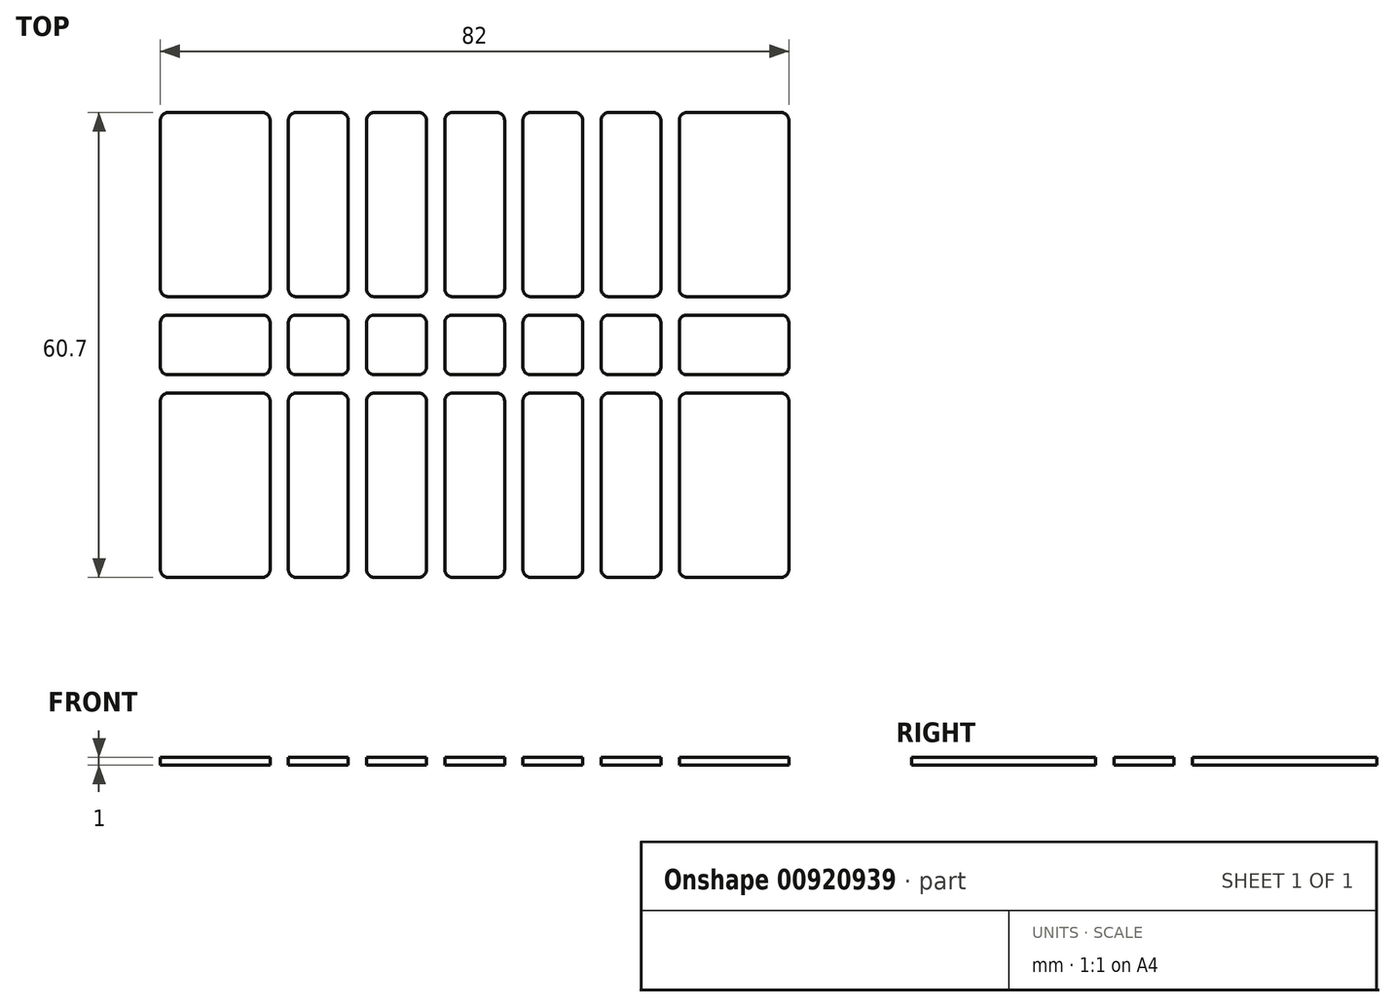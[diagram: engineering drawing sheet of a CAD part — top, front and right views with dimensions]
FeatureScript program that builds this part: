
annotation { "Feature Type Name" : "Feature", "Feature Type Description" : "" }
export const myFeature = defineFeature(function(context is Context, id is Id, definition is map)
    precondition{}
    {
        {
            var Q0;
            Q0=qCreatedBy(makeId("Top.planeOp"),FACE);
            var sketch = newSketch(context, id + "F0", { "sketchPlane" : qUnion([Q0])});
            skLineSegment(sketch, "E0.bottom", {"start": v(44, 33.35) * mm, "end": v(-44, 33.35) * mm, "construction": true});
            skLineSegment(sketch, "E0.top", {"start": v(44, -33.35) * mm, "end": v(-44, -33.35) * mm, "construction": true});
            skLineSegment(sketch, "E0.left", {"start": v(44, 33.35) * mm, "end": v(44, -33.35) * mm, "construction": true});
            skLineSegment(sketch, "E0.right", {"start": v(-44, 33.35) * mm, "end": v(-44, -33.35) * mm, "construction": true});
            skLineSegment(sketch, "E1", {"start": v(0, 0) * mm, "end": v(0, -33.35) * mm, "construction": true});
            skLineSegment(sketch, "E2", {"start": v(-5.1, 0) * mm, "end": v(-5.1, -33.35) * mm, "construction": true});
            skLineSegment(sketch, "E3", {"start": v(-15.3, 0) * mm, "end": v(-15.3, -33.35) * mm, "construction": true});
            skLineSegment(sketch, "E4", {"start": v(-25.5, 0) * mm, "end": v(-25.5, -33.35) * mm, "construction": true});
            skLineSegment(sketch, "E5.MirrorCS", {"start": v(5.1, 0) * mm, "end": v(5.1, -33.35) * mm, "construction": true});
            skLineSegment(sketch, "E6", {"start": v(0, 0) * mm, "end": v(-44, 0) * mm, "construction": true});
            skLineSegment(sketch, "E7", {"start": v(0, -5.1) * mm, "end": v(-44, -5.1) * mm, "construction": true});
            skLineSegment(sketch, "E8.MirrorCS", {"start": v(0, 5.1) * mm, "end": v(-44, 5.1) * mm, "construction": true});
            skLineSegment(sketch, "E9.bottom", {"start": v(-40, -6.3) * mm, "end": v(-27.7, -6.3) * mm});
            skLineSegment(sketch, "E9.top", {"start": v(-40, -30.35) * mm, "end": v(-27.7, -30.35) * mm});
            skLineSegment(sketch, "E9.left", {"start": v(-41, -7.3) * mm, "end": v(-41, -29.35) * mm});
            skLineSegment(sketch, "E9.right", {"start": v(-26.7, -7.3) * mm, "end": v(-26.7, -29.35) * mm});
            skLineSegment(sketch, "E10.bottom", {"start": v(-23.3, -6.3) * mm, "end": v(-17.5, -6.3) * mm});
            skLineSegment(sketch, "E10.top", {"start": v(-23.3, -30.35) * mm, "end": v(-17.5, -30.35) * mm});
            skLineSegment(sketch, "E10.left", {"start": v(-24.3, -7.3) * mm, "end": v(-24.3, -29.35) * mm});
            skLineSegment(sketch, "E10.right", {"start": v(-16.5, -7.3) * mm, "end": v(-16.5, -29.35) * mm});
            skLineSegment(sketch, "E11.bottom", {"start": v(-13.1, -6.3) * mm, "end": v(-7.3, -6.3) * mm});
            skLineSegment(sketch, "E11.top", {"start": v(-13.1, -30.35) * mm, "end": v(-7.3, -30.35) * mm});
            skLineSegment(sketch, "E11.left", {"start": v(-14.1, -7.3) * mm, "end": v(-14.1, -29.35) * mm});
            skLineSegment(sketch, "E11.right", {"start": v(-6.3, -7.3) * mm, "end": v(-6.3, -29.35) * mm});
            skLineSegment(sketch, "E12.bottom", {"start": v(-2.9, -6.3) * mm, "end": v(2.9, -6.3) * mm});
            skLineSegment(sketch, "E12.top", {"start": v(-2.9, -30.35) * mm, "end": v(2.9, -30.35) * mm});
            skLineSegment(sketch, "E12.left", {"start": v(-3.9, -7.3) * mm, "end": v(-3.9, -29.35) * mm});
            skLineSegment(sketch, "E12.right", {"start": v(3.9, -7.3) * mm, "end": v(3.9, -29.35) * mm});
            skLineSegment(sketch, "E13.bottom", {"start": v(-40, 3.9) * mm, "end": v(-27.7, 3.9) * mm});
            skLineSegment(sketch, "E13.top", {"start": v(-40, -3.9) * mm, "end": v(-27.7, -3.9) * mm});
            skLineSegment(sketch, "E13.left", {"start": v(-41, 2.9) * mm, "end": v(-41, -2.9) * mm});
            skLineSegment(sketch, "E13.right", {"start": v(-26.7, 2.9) * mm, "end": v(-26.7, -2.9) * mm});
            skLineSegment(sketch, "E14.bottom", {"start": v(-23.3, 3.9) * mm, "end": v(-17.5, 3.9) * mm});
            skLineSegment(sketch, "E14.top", {"start": v(-23.3, -3.9) * mm, "end": v(-17.5, -3.9) * mm});
            skLineSegment(sketch, "E14.left", {"start": v(-24.3, 2.9) * mm, "end": v(-24.3, -2.9) * mm});
            skLineSegment(sketch, "E14.right", {"start": v(-16.5, 2.9) * mm, "end": v(-16.5, -2.9) * mm});
            skLineSegment(sketch, "E15.bottom", {"start": v(-13.1, 3.9) * mm, "end": v(-7.3, 3.9) * mm});
            skLineSegment(sketch, "E15.top", {"start": v(-13.1, -3.9) * mm, "end": v(-7.3, -3.9) * mm});
            skLineSegment(sketch, "E15.left", {"start": v(-14.1, 2.9) * mm, "end": v(-14.1, -2.9) * mm});
            skLineSegment(sketch, "E15.right", {"start": v(-6.3, 2.9) * mm, "end": v(-6.3, -2.9) * mm});
            skLineSegment(sketch, "E16.bottom", {"start": v(-2.9, 3.9) * mm, "end": v(2.9, 3.9) * mm});
            skLineSegment(sketch, "E16.top", {"start": v(-2.9, -3.9) * mm, "end": v(2.9, -3.9) * mm});
            skLineSegment(sketch, "E16.left", {"start": v(-3.9, 2.9) * mm, "end": v(-3.9, -2.9) * mm});
            skLineSegment(sketch, "E16.right", {"start": v(3.9, 2.9) * mm, "end": v(3.9, -2.9) * mm});
            skPoint(sketch, "E17.visualSharp", {"position": v(-41, -30.35) * mm});
            skArc(sketch, "E17.filletArc", {"start": v(-41, -29.35) * mm, "mid": v(-40.7, -30.06) * mm, "end": v(-40, -30.35) * mm});
            skPoint(sketch, "E18.visualSharp", {"position": v(-26.7, -30.35) * mm});
            skArc(sketch, "E18.filletArc", {"start": v(-27.7, -30.35) * mm, "mid": v(-27, -30.06) * mm, "end": v(-26.7, -29.35) * mm});
            skPoint(sketch, "E19.visualSharp", {"position": v(-24.3, -30.35) * mm});
            skArc(sketch, "E19.filletArc", {"start": v(-24.3, -29.35) * mm, "mid": v(-24, -30.06) * mm, "end": v(-23.3, -30.35) * mm});
            skPoint(sketch, "E20.visualSharp", {"position": v(-16.5, -30.35) * mm});
            skArc(sketch, "E20.filletArc", {"start": v(-17.5, -30.35) * mm, "mid": v(-16.8, -30.06) * mm, "end": v(-16.5, -29.35) * mm});
            skPoint(sketch, "E21.visualSharp", {"position": v(-14.1, -30.35) * mm});
            skArc(sketch, "E21.filletArc", {"start": v(-14.1, -29.35) * mm, "mid": v(-13.8, -30.06) * mm, "end": v(-13.1, -30.35) * mm});
            skPoint(sketch, "E22.visualSharp", {"position": v(-6.3, -30.35) * mm});
            skArc(sketch, "E22.filletArc", {"start": v(-7.3, -30.35) * mm, "mid": v(-6.6, -30.06) * mm, "end": v(-6.3, -29.35) * mm});
            skPoint(sketch, "E23.visualSharp", {"position": v(-3.9, -30.35) * mm});
            skArc(sketch, "E23.filletArc", {"start": v(-3.9, -29.35) * mm, "mid": v(-3.6, -30.06) * mm, "end": v(-2.9, -30.35) * mm});
            skPoint(sketch, "E24.visualSharp", {"position": v(3.9, -30.35) * mm});
            skArc(sketch, "E24.filletArc", {"start": v(2.9, -30.35) * mm, "mid": v(3.6, -30.06) * mm, "end": v(3.9, -29.35) * mm});
            skPoint(sketch, "E25.visualSharp", {"position": v(3.9, -6.3) * mm});
            skArc(sketch, "E25.filletArc", {"start": v(3.9, -7.3) * mm, "mid": v(3.6, -6.6) * mm, "end": v(2.9, -6.3) * mm});
            skPoint(sketch, "E26.visualSharp", {"position": v(-3.9, -6.3) * mm});
            skArc(sketch, "E26.filletArc", {"start": v(-2.9, -6.3) * mm, "mid": v(-3.6, -6.6) * mm, "end": v(-3.9, -7.3) * mm});
            skPoint(sketch, "E27.visualSharp", {"position": v(-6.3, -6.3) * mm});
            skArc(sketch, "E27.filletArc", {"start": v(-6.3, -7.3) * mm, "mid": v(-6.6, -6.6) * mm, "end": v(-7.3, -6.3) * mm});
            skPoint(sketch, "E28.visualSharp", {"position": v(-14.1, -6.3) * mm});
            skArc(sketch, "E28.filletArc", {"start": v(-13.1, -6.3) * mm, "mid": v(-13.8, -6.6) * mm, "end": v(-14.1, -7.3) * mm});
            skPoint(sketch, "E29.visualSharp", {"position": v(-16.5, -6.3) * mm});
            skArc(sketch, "E29.filletArc", {"start": v(-16.5, -7.3) * mm, "mid": v(-16.8, -6.6) * mm, "end": v(-17.5, -6.3) * mm});
            skPoint(sketch, "E30.visualSharp", {"position": v(-24.3, -6.3) * mm});
            skArc(sketch, "E30.filletArc", {"start": v(-23.3, -6.3) * mm, "mid": v(-24, -6.6) * mm, "end": v(-24.3, -7.3) * mm});
            skPoint(sketch, "E31.visualSharp", {"position": v(-26.7, -6.3) * mm});
            skArc(sketch, "E31.filletArc", {"start": v(-26.7, -7.3) * mm, "mid": v(-27, -6.6) * mm, "end": v(-27.7, -6.3) * mm});
            skPoint(sketch, "E32.visualSharp", {"position": v(-41, -6.3) * mm});
            skArc(sketch, "E32.filletArc", {"start": v(-40, -6.3) * mm, "mid": v(-40.7, -6.6) * mm, "end": v(-41, -7.3) * mm});
            skPoint(sketch, "E33.visualSharp", {"position": v(-41, -3.9) * mm});
            skArc(sketch, "E33.filletArc", {"start": v(-41, -2.9) * mm, "mid": v(-40.7, -3.6) * mm, "end": v(-40, -3.9) * mm});
            skPoint(sketch, "E34.visualSharp", {"position": v(-26.7, -3.9) * mm});
            skArc(sketch, "E34.filletArc", {"start": v(-27.7, -3.9) * mm, "mid": v(-27, -3.6) * mm, "end": v(-26.7, -2.9) * mm});
            skPoint(sketch, "E35.visualSharp", {"position": v(-24.3, -3.9) * mm});
            skArc(sketch, "E35.filletArc", {"start": v(-24.3, -2.9) * mm, "mid": v(-24, -3.6) * mm, "end": v(-23.3, -3.9) * mm});
            skPoint(sketch, "E36.visualSharp", {"position": v(-16.5, -3.9) * mm});
            skArc(sketch, "E36.filletArc", {"start": v(-17.5, -3.9) * mm, "mid": v(-16.8, -3.6) * mm, "end": v(-16.5, -2.9) * mm});
            skPoint(sketch, "E37.visualSharp", {"position": v(-14.1, -3.9) * mm});
            skArc(sketch, "E37.filletArc", {"start": v(-14.1, -2.9) * mm, "mid": v(-13.8, -3.6) * mm, "end": v(-13.1, -3.9) * mm});
            skPoint(sketch, "E38.visualSharp", {"position": v(-6.3, -3.9) * mm});
            skArc(sketch, "E38.filletArc", {"start": v(-7.3, -3.9) * mm, "mid": v(-6.6, -3.6) * mm, "end": v(-6.3, -2.9) * mm});
            skPoint(sketch, "E39.visualSharp", {"position": v(-3.9, -3.9) * mm});
            skArc(sketch, "E39.filletArc", {"start": v(-3.9, -2.9) * mm, "mid": v(-3.6, -3.6) * mm, "end": v(-2.9, -3.9) * mm});
            skPoint(sketch, "E40.visualSharp", {"position": v(3.9, -3.9) * mm});
            skArc(sketch, "E40.filletArc", {"start": v(2.9, -3.9) * mm, "mid": v(3.6, -3.6) * mm, "end": v(3.9, -2.9) * mm});
            skPoint(sketch, "E41.visualSharp", {"position": v(3.9, 3.9) * mm});
            skArc(sketch, "E41.filletArc", {"start": v(3.9, 2.9) * mm, "mid": v(3.6, 3.6) * mm, "end": v(2.9, 3.9) * mm});
            skPoint(sketch, "E42.visualSharp", {"position": v(-3.9, 3.9) * mm});
            skArc(sketch, "E42.filletArc", {"start": v(-2.9, 3.9) * mm, "mid": v(-3.6, 3.6) * mm, "end": v(-3.9, 2.9) * mm});
            skPoint(sketch, "E43.visualSharp", {"position": v(-6.3, 3.9) * mm});
            skArc(sketch, "E43.filletArc", {"start": v(-6.3, 2.9) * mm, "mid": v(-6.6, 3.6) * mm, "end": v(-7.3, 3.9) * mm});
            skPoint(sketch, "E44.visualSharp", {"position": v(-14.1, 3.9) * mm});
            skArc(sketch, "E44.filletArc", {"start": v(-13.1, 3.9) * mm, "mid": v(-13.8, 3.6) * mm, "end": v(-14.1, 2.9) * mm});
            skPoint(sketch, "E45.visualSharp", {"position": v(-16.5, 3.9) * mm});
            skArc(sketch, "E45.filletArc", {"start": v(-16.5, 2.9) * mm, "mid": v(-16.8, 3.6) * mm, "end": v(-17.5, 3.9) * mm});
            skPoint(sketch, "E46.visualSharp", {"position": v(-24.3, 3.9) * mm});
            skArc(sketch, "E46.filletArc", {"start": v(-23.3, 3.9) * mm, "mid": v(-24, 3.6) * mm, "end": v(-24.3, 2.9) * mm});
            skPoint(sketch, "E47.visualSharp", {"position": v(-26.7, 3.9) * mm});
            skArc(sketch, "E47.filletArc", {"start": v(-26.7, 2.9) * mm, "mid": v(-27, 3.6) * mm, "end": v(-27.7, 3.9) * mm});
            skPoint(sketch, "E48.visualSharp", {"position": v(-41, 3.9) * mm});
            skArc(sketch, "E48.filletArc", {"start": v(-40, 3.9) * mm, "mid": v(-40.7, 3.6) * mm, "end": v(-41, 2.9) * mm});
            skSolve(sketch);
        }
        {
            var Q0;
            Q0=qSketchRegion(id+"F0",true);
            extrude(context, id + "F1", {"entities" : qUnion([Q0]), "depth" : 1 * mm, "offsetDistance" : 25 * mm});
        }
        {
            var Q0;
            Q0=makeQuery(id+"F1.opExtrude","SWEPT_BODY",BODY,{"disambiguationData":[OSD([sQuery(id+"F0.wireOp",EDGE,"E9.bottom"),sQuery(id+"F0.wireOp",EDGE,"E9.top"),sQuery(id+"F0.wireOp",EDGE,"E9.left"),sQuery(id+"F0.wireOp",EDGE,"E9.right"),sQuery(id+"F0.wireOp",EDGE,"E17.filletArc"),sQuery(id+"F0.wireOp",EDGE,"E18.filletArc"),sQuery(id+"F0.wireOp",EDGE,"E31.filletArc"),sQuery(id+"F0.wireOp",EDGE,"E32.filletArc")])]});
            var Q1;
            Q1=makeQuery(id+"F1.opExtrude","SWEPT_BODY",BODY,{"disambiguationData":[OSD([sQuery(id+"F0.wireOp",EDGE,"E10.bottom"),sQuery(id+"F0.wireOp",EDGE,"E10.top"),sQuery(id+"F0.wireOp",EDGE,"E10.left"),sQuery(id+"F0.wireOp",EDGE,"E10.right"),sQuery(id+"F0.wireOp",EDGE,"E19.filletArc"),sQuery(id+"F0.wireOp",EDGE,"E20.filletArc"),sQuery(id+"F0.wireOp",EDGE,"E29.filletArc"),sQuery(id+"F0.wireOp",EDGE,"E30.filletArc")])]});
            var Q2;
            Q2=makeQuery(id+"F1.opExtrude","SWEPT_BODY",BODY,{"disambiguationData":[OSD([sQuery(id+"F0.wireOp",EDGE,"E11.bottom"),sQuery(id+"F0.wireOp",EDGE,"E11.top"),sQuery(id+"F0.wireOp",EDGE,"E11.left"),sQuery(id+"F0.wireOp",EDGE,"E11.right"),sQuery(id+"F0.wireOp",EDGE,"E21.filletArc"),sQuery(id+"F0.wireOp",EDGE,"E22.filletArc"),sQuery(id+"F0.wireOp",EDGE,"E27.filletArc"),sQuery(id+"F0.wireOp",EDGE,"E28.filletArc")])]});
            var Q3;
            Q3=makeQuery(id+"F1.opExtrude","SWEPT_BODY",BODY,{"disambiguationData":[OSD([sQuery(id+"F0.wireOp",EDGE,"E12.bottom"),sQuery(id+"F0.wireOp",EDGE,"E12.top"),sQuery(id+"F0.wireOp",EDGE,"E12.left"),sQuery(id+"F0.wireOp",EDGE,"E12.right"),sQuery(id+"F0.wireOp",EDGE,"E23.filletArc"),sQuery(id+"F0.wireOp",EDGE,"E24.filletArc"),sQuery(id+"F0.wireOp",EDGE,"E25.filletArc"),sQuery(id+"F0.wireOp",EDGE,"E26.filletArc")])]});
            var Q4;
            Q4=qCreatedBy(makeId("Front.planeOp"),FACE);
            mirror(context, id + "F2", {"entities" : qUnion([Q0, Q1, Q2, Q3]), "mirrorPlane" : qUnion([Q4])});
        }
        {
            var Q0;
            Q0=makeQuery(id+"F2.opPattern","COPY",BODY,{"derivedFrom":makeQuery(id+"F1.opExtrude","SWEPT_BODY",BODY,{"disambiguationData":[OSD([sQuery(id+"F0.wireOp",EDGE,"E9.bottom"),sQuery(id+"F0.wireOp",EDGE,"E9.top"),sQuery(id+"F0.wireOp",EDGE,"E9.left"),sQuery(id+"F0.wireOp",EDGE,"E9.right"),sQuery(id+"F0.wireOp",EDGE,"E17.filletArc"),sQuery(id+"F0.wireOp",EDGE,"E18.filletArc"),sQuery(id+"F0.wireOp",EDGE,"E31.filletArc"),sQuery(id+"F0.wireOp",EDGE,"E32.filletArc")])]}),"instanceName":"1"});
            var Q1;
            Q1=makeQuery(id+"F2.opPattern","COPY",BODY,{"derivedFrom":makeQuery(id+"F1.opExtrude","SWEPT_BODY",BODY,{"disambiguationData":[OSD([sQuery(id+"F0.wireOp",EDGE,"E10.bottom"),sQuery(id+"F0.wireOp",EDGE,"E10.top"),sQuery(id+"F0.wireOp",EDGE,"E10.left"),sQuery(id+"F0.wireOp",EDGE,"E10.right"),sQuery(id+"F0.wireOp",EDGE,"E19.filletArc"),sQuery(id+"F0.wireOp",EDGE,"E20.filletArc"),sQuery(id+"F0.wireOp",EDGE,"E29.filletArc"),sQuery(id+"F0.wireOp",EDGE,"E30.filletArc")])]}),"instanceName":"1"});
            var Q2;
            Q2=makeQuery(id+"F2.opPattern","COPY",BODY,{"derivedFrom":makeQuery(id+"F1.opExtrude","SWEPT_BODY",BODY,{"disambiguationData":[OSD([sQuery(id+"F0.wireOp",EDGE,"E11.bottom"),sQuery(id+"F0.wireOp",EDGE,"E11.top"),sQuery(id+"F0.wireOp",EDGE,"E11.left"),sQuery(id+"F0.wireOp",EDGE,"E11.right"),sQuery(id+"F0.wireOp",EDGE,"E21.filletArc"),sQuery(id+"F0.wireOp",EDGE,"E22.filletArc"),sQuery(id+"F0.wireOp",EDGE,"E27.filletArc"),sQuery(id+"F0.wireOp",EDGE,"E28.filletArc")])]}),"instanceName":"1"});
            var Q3;
            Q3=makeQuery(id+"F1.opExtrude","SWEPT_BODY",BODY,{"disambiguationData":[OSD([sQuery(id+"F0.wireOp",EDGE,"E15.bottom"),sQuery(id+"F0.wireOp",EDGE,"E15.top"),sQuery(id+"F0.wireOp",EDGE,"E15.left"),sQuery(id+"F0.wireOp",EDGE,"E15.right"),sQuery(id+"F0.wireOp",EDGE,"E37.filletArc"),sQuery(id+"F0.wireOp",EDGE,"E38.filletArc"),sQuery(id+"F0.wireOp",EDGE,"E43.filletArc"),sQuery(id+"F0.wireOp",EDGE,"E44.filletArc")])]});
            var Q4;
            Q4=makeQuery(id+"F1.opExtrude","SWEPT_BODY",BODY,{"disambiguationData":[OSD([sQuery(id+"F0.wireOp",EDGE,"E14.bottom"),sQuery(id+"F0.wireOp",EDGE,"E14.top"),sQuery(id+"F0.wireOp",EDGE,"E14.left"),sQuery(id+"F0.wireOp",EDGE,"E14.right"),sQuery(id+"F0.wireOp",EDGE,"E35.filletArc"),sQuery(id+"F0.wireOp",EDGE,"E36.filletArc"),sQuery(id+"F0.wireOp",EDGE,"E45.filletArc"),sQuery(id+"F0.wireOp",EDGE,"E46.filletArc")])]});
            var Q5;
            Q5=makeQuery(id+"F1.opExtrude","SWEPT_BODY",BODY,{"disambiguationData":[OSD([sQuery(id+"F0.wireOp",EDGE,"E13.bottom"),sQuery(id+"F0.wireOp",EDGE,"E13.top"),sQuery(id+"F0.wireOp",EDGE,"E13.left"),sQuery(id+"F0.wireOp",EDGE,"E13.right"),sQuery(id+"F0.wireOp",EDGE,"E33.filletArc"),sQuery(id+"F0.wireOp",EDGE,"E34.filletArc"),sQuery(id+"F0.wireOp",EDGE,"E47.filletArc"),sQuery(id+"F0.wireOp",EDGE,"E48.filletArc")])]});
            var Q6;
            Q6=makeQuery(id+"F1.opExtrude","SWEPT_BODY",BODY,{"disambiguationData":[OSD([sQuery(id+"F0.wireOp",EDGE,"E9.bottom"),sQuery(id+"F0.wireOp",EDGE,"E9.top"),sQuery(id+"F0.wireOp",EDGE,"E9.left"),sQuery(id+"F0.wireOp",EDGE,"E9.right"),sQuery(id+"F0.wireOp",EDGE,"E17.filletArc"),sQuery(id+"F0.wireOp",EDGE,"E18.filletArc"),sQuery(id+"F0.wireOp",EDGE,"E31.filletArc"),sQuery(id+"F0.wireOp",EDGE,"E32.filletArc")])]});
            var Q7;
            Q7=makeQuery(id+"F1.opExtrude","SWEPT_BODY",BODY,{"disambiguationData":[OSD([sQuery(id+"F0.wireOp",EDGE,"E10.bottom"),sQuery(id+"F0.wireOp",EDGE,"E10.top"),sQuery(id+"F0.wireOp",EDGE,"E10.left"),sQuery(id+"F0.wireOp",EDGE,"E10.right"),sQuery(id+"F0.wireOp",EDGE,"E19.filletArc"),sQuery(id+"F0.wireOp",EDGE,"E20.filletArc"),sQuery(id+"F0.wireOp",EDGE,"E29.filletArc"),sQuery(id+"F0.wireOp",EDGE,"E30.filletArc")])]});
            var Q8;
            Q8=makeQuery(id+"F1.opExtrude","SWEPT_BODY",BODY,{"disambiguationData":[OSD([sQuery(id+"F0.wireOp",EDGE,"E11.bottom"),sQuery(id+"F0.wireOp",EDGE,"E11.top"),sQuery(id+"F0.wireOp",EDGE,"E11.left"),sQuery(id+"F0.wireOp",EDGE,"E11.right"),sQuery(id+"F0.wireOp",EDGE,"E21.filletArc"),sQuery(id+"F0.wireOp",EDGE,"E22.filletArc"),sQuery(id+"F0.wireOp",EDGE,"E27.filletArc"),sQuery(id+"F0.wireOp",EDGE,"E28.filletArc")])]});
            var Q9;
            Q9=qCreatedBy(makeId("Right.planeOp"),FACE);
            mirror(context, id + "F3", {"entities" : qUnion([Q0, Q1, Q2, Q3, Q4, Q5, Q6, Q7, Q8]), "mirrorPlane" : qUnion([Q9])});
        }
    });
